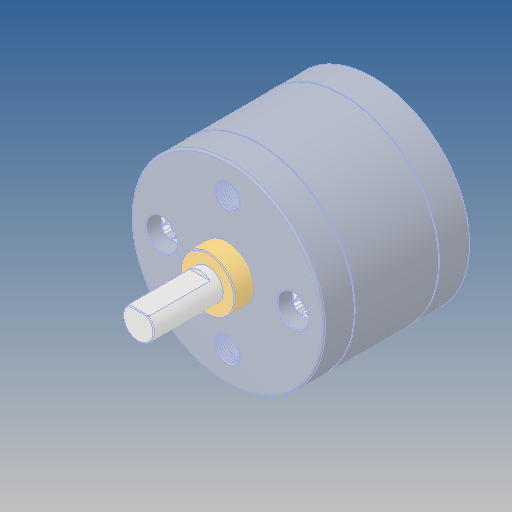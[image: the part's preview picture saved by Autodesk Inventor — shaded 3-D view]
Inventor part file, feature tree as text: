
AUTODESK INVENTOR PART (.ipt)
format: ipt  version: 2020 (Build 240168000, 168)  size: 714,752 bytes
history: mixed  units: mm
features: other x1, fillet x1, imported_body x1
ambient origin geometry x8: Origin, YZ Plane, XZ Plane, XY Plane, X Axis, Y Axis, Z Axis, Center Point
bodies: Body1 (imported_parasolid)
feature tree (3):
  other  "Твердое тело1"
  fillet  "Fillet2"  [1 undecoded]
  imported_body  NMx_Import_Brep_tag  [imported B-rep: ~6 faces, bbox_mm=None]
note: 1 required parameter value undecoded (feature->parameter linkage not recoverable at this tier; creation-order binding heuristic only, values carry confidence <= 0.55)
